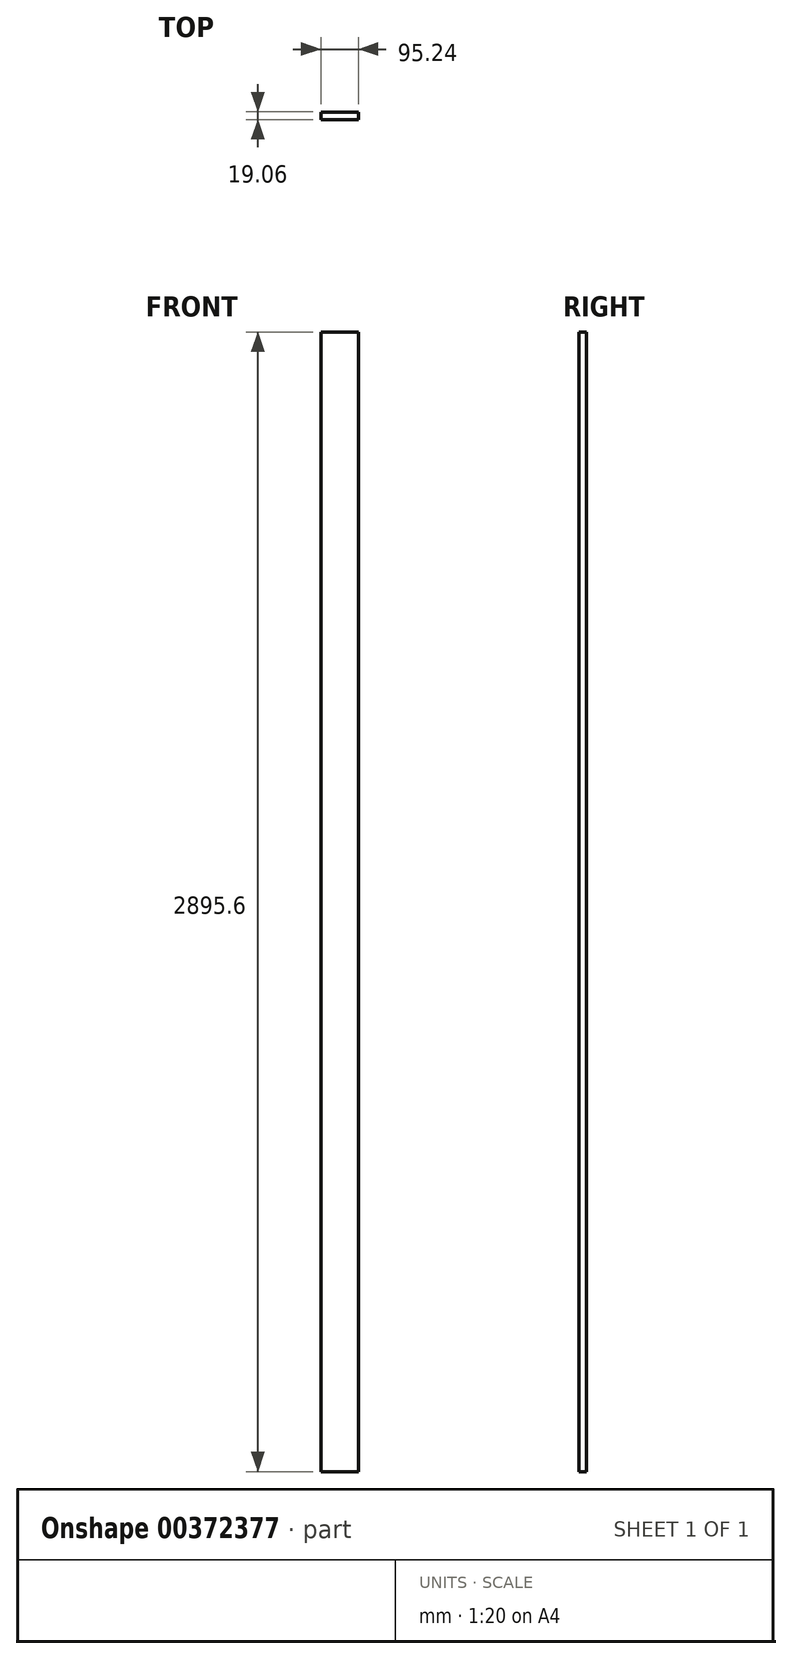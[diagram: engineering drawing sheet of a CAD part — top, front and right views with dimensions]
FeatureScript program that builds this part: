
annotation { "Feature Type Name" : "Feature", "Feature Type Description" : "" }
export const myFeature = defineFeature(function(context is Context, id is Id, definition is map)
    precondition{}
    {
        {
            var Q0;
            Q0=qCreatedBy(makeId("Top.planeOp"),FACE);
            var sketch = newSketch(context, id + "F0", { "sketchPlane" : qUnion([Q0])});
            skLineSegment(sketch, "E0.bottom", {"start": v(-47.62, 9.53) * mm, "end": v(47.63, 9.53) * mm});
            skLineSegment(sketch, "E0.top", {"start": v(-47.62, -9.53) * mm, "end": v(47.63, -9.53) * mm});
            skLineSegment(sketch, "E0.left", {"start": v(-47.62, 9.53) * mm, "end": v(-47.62, -9.52) * mm});
            skLineSegment(sketch, "E0.right", {"start": v(47.63, 9.53) * mm, "end": v(47.63, -9.52) * mm});
            skPoint(sketch, "E0.middle", {"position": v(0, 0) * mm});
            skSolve(sketch);
        }
        {
            var Q0;
            Q0 = qSketchRegion(id + "F0", true);
            extrude(context, id + "F1", {"entities" : qUnion([Q0]), "endBound" : BoundingType.SYMMETRIC, "depth" : 2895.6 * mm});
        }
    });
